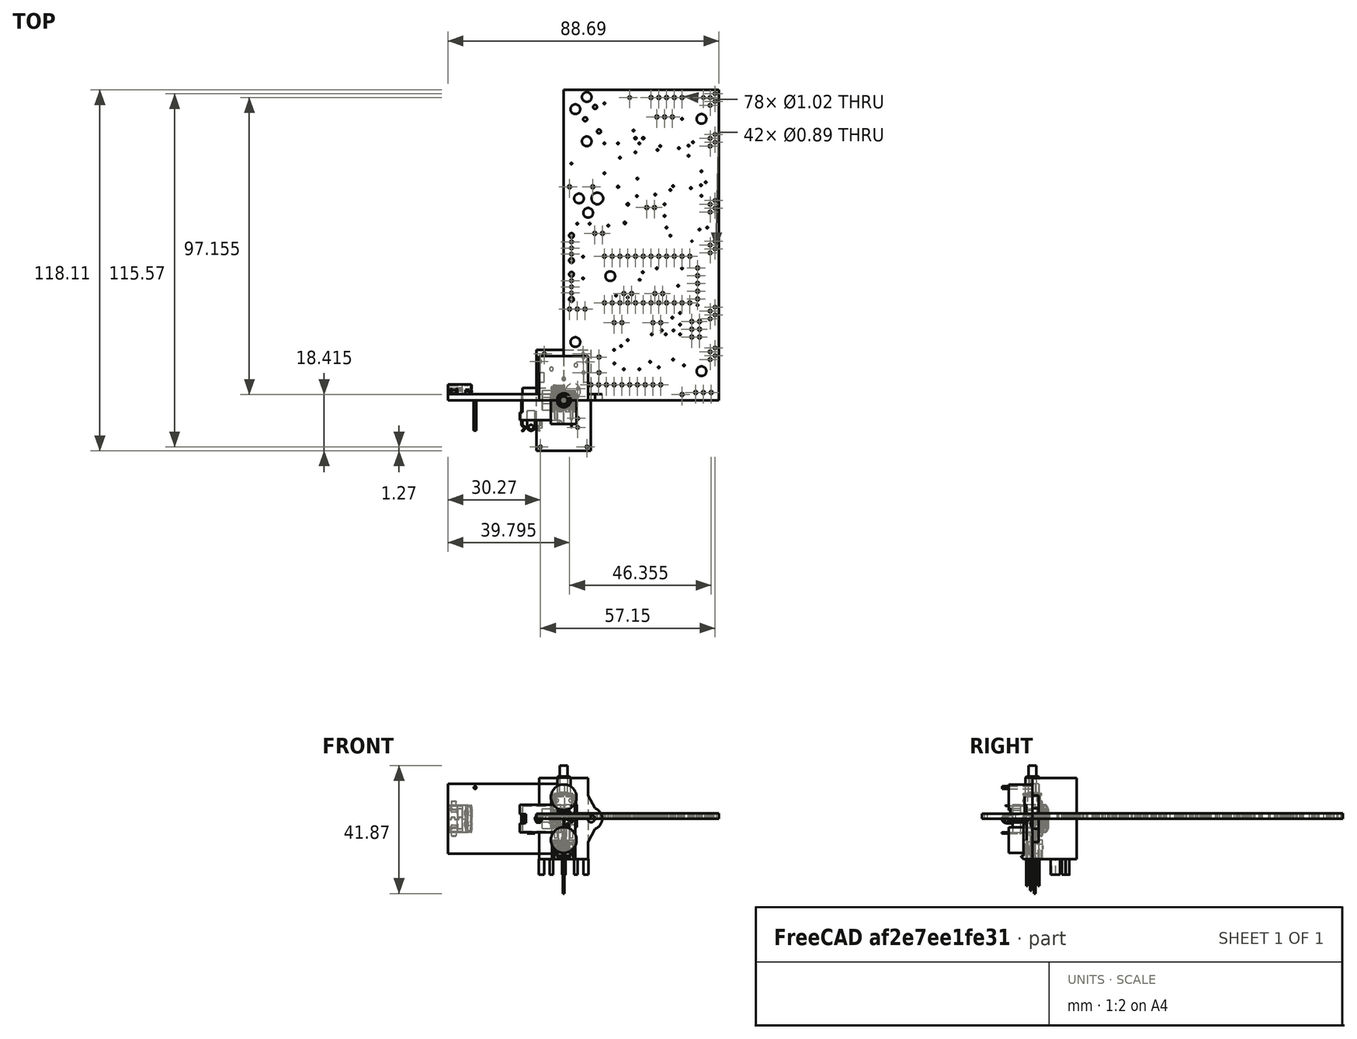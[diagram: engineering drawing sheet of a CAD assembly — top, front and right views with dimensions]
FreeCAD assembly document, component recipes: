
FREECAD ASSEMBLY — COMPONENT RECIPES ("PCB")

This assembly document has 17 components, labeled P0..P16 below (a component is one placed body or linked part). 2 of them carry a construction recipe — the FreeCAD feature program that regenerates the part from scratch, quoted from this document or its linked companion documents; the rest are supplied as boundary geometry only. No exploded tour is included for this assembly.
COMPONENT P0 — geometry summary ("CUI_PJ-202A001"; no construction recipe available for this part):
  bounding box: 14.5 x 14.4 x 9.4 mm
  tessellated surface: 3,812 triangles
  volume: 1019 mm^3 (52% of its bounding box)
COMPONENT P1 — geometry summary ("Dual RCA001"; no construction recipe available for this part):
  bounding box: 31.6 x 22.3 x 20.7 mm
  tessellated surface: 2,744 triangles
  volume: 7146 mm^3 (49% of its bounding box)
COMPONENT P2 — recipe-attached ("Ft232H-2-assembly001", modeled in this document).
Construction recipe (the document's own serialized feature program — sketch geometry with constraints, then the solid features built on it; lengths are millimeters unless a unit is written):

FEATURE [PartDesign::SubShapeBinder] Binder
  BindCopyOnChange = 0
  BindMode = 0
  ClaimChildren = false
  Context = -> Assembly [Ft232H_2_assembly001.Body001.Binder.]
  Fuse = false
  MakeFace = true
  OffsetFill = false
  OffsetIntersection = false
  OffsetJoinType = 0
  OffsetOpenResult = false
  PartialLoad = false
  Refine = true
  Relative = true
  Support = -> [Part__Feature016]
  _Version = 2
FEATURE [Sketcher::SketchObject] Sketch
  ArcFitTolerance = 1e-06
  AttachmentSupport = -> [Binder]
  ExternalGeometry = -> [Binder]
  FullyConstrained = true
  MakeInternals = false
  MapMode = 5
  Placement = pos=(0,-1.32e-13,0) rot=(1,0,0;1.5708rad)
  sketch-geometry (10):
    g0: LineSegment [constr] StartX=-31.5438 StartY=10.16 StartZ=0 EndX=-31.5438 EndY=-10.16 EndZ=0
    g1: LineSegment [constr] StartX=-31.5438 StartY=-10.16 StartZ=0 EndX=-6.14378 EndY=-10.16 EndZ=0
    g2: LineSegment [constr] StartX=-6.14378 StartY=-10.16 StartZ=0 EndX=-6.14378 EndY=10.16 EndZ=0
    g3: LineSegment [constr] StartX=-6.14378 StartY=10.16 StartZ=0 EndX=-31.5438 EndY=10.16 EndZ=0
    g4: GeomPoint [constr] X=-37.8938 Y=-3.968e-13 Z=0
    g5: GeomPoint [constr] X=-31.5438 Y=-3.968e-13 Z=0
    g6: GeomPoint [constr] X=-18.8438 Y=11.43 Z=0
    g7: GeomPoint [constr] X=-18.8438 Y=10.16 Z=0
    g8: Circle [constr] CenterX=-31.5438 CenterY=10.16 CenterZ=0 NormalX=0 NormalY=0 NormalZ=1 AngleXU=0 Radius=0.4445
    g9: Circle CenterX=-29.0038 CenterY=10.16 CenterZ=0 NormalX=0 NormalY=0 NormalZ=1 AngleXU=0 Radius=0.4445
  constraints (23):
    c: DistanceX(g-3,g-1) = 37.8938
    c: Distance(g-3,g-4) = 22.86
    c: Coincident(g1,g2)
    c: Coincident(g2,g3)
    c: Coincident(g3,g0)
    c: Vertical(g0)
    c: Vertical(g2)
    c: Horizontal(g1)
    c: Horizontal(g3)
    c: DistanceX(g3,g3) = 25.4
    c: DistanceY(g2,g2) = 20.32
    c: Symmetric(g-3,g-4,g4)
    c: Symmetric(g0,g0,g5)
    c: Horizontal(g5,g4)
    c: Symmetric(g2,g0,g7)
    c: Symmetric(g-3,g-3,g6)
    c: Vertical(g7,g6)
    c: Coincident(g8,g0)
    c: Diameter(g8) = 0.889
    c: Coincident(g1,g0)
    c: Horizontal(g0,g9)
    c: DistanceX(g0,g9) = 2.54
    c: Equal(g8,g9)
FEATURE [PartDesign::Pad] Pad
  Direction = (0,-1,2e-16)
  Length = 9.906
  Length2 = 10
  Profile = -> Sketch
  ReferenceAxis = -> Sketch [N_Axis]
  Refine = true
  Suppressed = false
  Type = 0
FEATURE [PartDesign::Body] Body001  label="Body"
  AllowCompound = false
  Group = -> [Binder,Sketch,Pad]
  Origin = -> Origin005
  Tip = -> Pad
COMPONENT P3 — geometry summary ("Pro Mini001"; no construction recipe available for this part):
  bounding box: 33.0 x 17.8 x 1.6 mm
  tessellated surface: 2,692 triangles
  volume: 922 mm^3 (99% of its bounding box)
  symmetry: mirror-symmetric across its z mid-plane
COMPONENT P4 — geometry summary ("SLW-864547-5A-RA-D001"; no construction recipe available for this part):
  bounding box: 9.5 x 8.6 x 7.5 mm
  tessellated surface: 1,292 triangles
  volume: 198 mm^3 (32% of its bounding box)
COMPONENT P5 — geometry summary ("SLW-864547-5A-RA-D002"; no construction recipe available for this part):
  bounding box: 9.5 x 8.6 x 7.5 mm
  tessellated surface: 1,292 triangles
  volume: 198 mm^3 (32% of its bounding box)
COMPONENT P6 — geometry summary ("SPST-momentary001"; no construction recipe available for this part):
  bounding box: 18.8 x 11.8 x 8.1 mm
  tessellated surface: 16,178 triangles
  volume: 314 mm^3 (17% of its bounding box)
COMPONENT P7 — geometry summary ("WP154A4SUREQBFZGC001"; no construction recipe available for this part):
  bounding box: 33.1 x 5.9 x 5.4 mm
  tessellated surface: 10,712 triangles
  volume: 191 mm^3 (18% of its bounding box)
  symmetry: mirror-symmetric across its z mid-plane
COMPONENT P8 — geometry summary ("WP154A4SUREQBFZGC002"; no construction recipe available for this part):
  bounding box: 33.1 x 5.9 x 5.4 mm
  tessellated surface: 10,712 triangles
  volume: 191 mm^3 (18% of its bounding box)
  symmetry: mirror-symmetric across its z mid-plane
COMPONENT P9 — geometry summary ("WP154A4SUREQBFZGC003"; no construction recipe available for this part):
  bounding box: 33.1 x 5.9 x 5.4 mm
  tessellated surface: 10,712 triangles
  volume: 191 mm^3 (18% of its bounding box)
  symmetry: mirror-symmetric across its z mid-plane
COMPONENT P10 — geometry summary ("WP154A4SUREQBFZGC004"; no construction recipe available for this part):
  bounding box: 33.1 x 5.9 x 5.4 mm
  tessellated surface: 10,712 triangles
  volume: 191 mm^3 (18% of its bounding box)
  symmetry: mirror-symmetric across its z mid-plane
COMPONENT P11 — geometry summary ("WP154A4SUREQBFZGC005"; no construction recipe available for this part):
  bounding box: 33.1 x 5.9 x 5.4 mm
  tessellated surface: 10,712 triangles
  volume: 191 mm^3 (18% of its bounding box)
  symmetry: mirror-symmetric across its z mid-plane
COMPONENT P12 — geometry summary ("WP154A4SUREQBFZGC006"; no construction recipe available for this part):
  bounding box: 33.1 x 5.9 x 5.4 mm
  tessellated surface: 10,712 triangles
  volume: 191 mm^3 (18% of its bounding box)
  symmetry: mirror-symmetric across its z mid-plane
COMPONENT P13 — geometry summary ("3pinconnector-640441-005"; no construction recipe available for this part):
  bounding box: 13.2 x 7.6 x 7.1 mm
  tessellated surface: 3,348 triangles
  volume: 338 mm^3 (47% of its bounding box)
COMPONENT P14 — geometry summary ("3pinconnector-640441-006"; no construction recipe available for this part):
  bounding box: 13.2 x 7.6 x 7.1 mm
  tessellated surface: 3,348 triangles
  volume: 338 mm^3 (47% of its bounding box)
COMPONENT P15 — geometry summary ("3pinconnector-640441-004"; no construction recipe available for this part):
  bounding box: 13.2 x 7.6 x 7.1 mm
  tessellated surface: 3,348 triangles
  volume: 338 mm^3 (47% of its bounding box)
COMPONENT P16 — recipe-attached ("pcb imported001", modeled in this document).
Construction recipe (the document's own serialized feature program — sketch geometry with constraints, then the solid features built on it; lengths are millimeters unless a unit is written):

FEATURE [Sketcher::SketchObject] MainSketch
  ArcFitTolerance = 1e-06
  AttachmentSupport = -> [XY_Plane]
  FullyConstrained = false
  MakeInternals = false
  MapMode = 5
  sketch-geometry (4):
    g0: LineSegment StartX=0 StartY=0 StartZ=0 EndX=50.8 EndY=0 EndZ=0
    g1: LineSegment StartX=50.8 StartY=0 StartZ=0 EndX=50.8 EndY=101.6 EndZ=0
    g2: LineSegment StartX=50.8 StartY=101.6 StartZ=0 EndX=0 EndY=101.6 EndZ=0
    g3: LineSegment StartX=0 StartY=101.6 StartZ=0 EndX=0 EndY=0 EndZ=0
  constraints (4):
    c: Horizontal(g0)
    c: Horizontal(g2)
    c: Vertical(g1)
    c: Vertical(g3)
FEATURE [PartDesign::Pad] Main
  Direction = (0,0,1)
  Length = 1.778
  Length2 = 100.076
  Profile = -> MainSketch
  Refine = true
  Suppressed = false
  Type = 0
FEATURE [Sketcher::SketchObject] HoleSketch
  ArcFitTolerance = 1e-06
  AttachmentSupport = -> [XY_Plane]
  FullyConstrained = false
  MakeInternals = false
  MapMode = 5
  sketch-geometry (197):
    g0: Circle CenterX=41.275 CenterY=47.117 CenterZ=0 NormalX=0 NormalY=0 NormalZ=1 AngleXU=0 Radius=0.508
    g1: Circle CenterX=38.735 CenterY=47.117 CenterZ=0 NormalX=0 NormalY=0 NormalZ=1 AngleXU=0 Radius=0.508
    g2: Circle CenterX=36.195 CenterY=47.117 CenterZ=0 NormalX=0 NormalY=0 NormalZ=1 AngleXU=0 Radius=0.508
    g3: Circle CenterX=13.335 CenterY=47.117 CenterZ=0 NormalX=0 NormalY=0 NormalZ=1 AngleXU=0 Radius=0.508
    g4: Circle CenterX=33.655 CenterY=47.117 CenterZ=0 NormalX=0 NormalY=0 NormalZ=1 AngleXU=0 Radius=0.508
    g5: Circle CenterX=15.875 CenterY=47.117 CenterZ=0 NormalX=0 NormalY=0 NormalZ=1 AngleXU=0 Radius=0.508
    g6: Circle CenterX=31.115 CenterY=47.117 CenterZ=0 NormalX=0 NormalY=0 NormalZ=1 AngleXU=0 Radius=0.508
    g7: Circle CenterX=28.575 CenterY=47.117 CenterZ=0 NormalX=0 NormalY=0 NormalZ=1 AngleXU=0 Radius=0.508
    g8: Circle CenterX=26.035 CenterY=47.117 CenterZ=0 NormalX=0 NormalY=0 NormalZ=1 AngleXU=0 Radius=0.508
    g9: Circle CenterX=18.415 CenterY=47.117 CenterZ=0 NormalX=0 NormalY=0 NormalZ=1 AngleXU=0 Radius=0.508
    g10: Circle CenterX=20.955 CenterY=47.117 CenterZ=0 NormalX=0 NormalY=0 NormalZ=1 AngleXU=0 Radius=0.508
    g11: Circle CenterX=23.495 CenterY=47.117 CenterZ=0 NormalX=0 NormalY=0 NormalZ=1 AngleXU=0 Radius=0.508
    g12: Circle CenterX=15.875 CenterY=31.877 CenterZ=0 NormalX=0 NormalY=0 NormalZ=1 AngleXU=0 Radius=0.508
    g13: Circle CenterX=13.335 CenterY=31.877 CenterZ=0 NormalX=0 NormalY=0 NormalZ=1 AngleXU=0 Radius=0.508
    g14: Circle CenterX=20.955 CenterY=31.877 CenterZ=0 NormalX=0 NormalY=0 NormalZ=1 AngleXU=0 Radius=0.508
    g15: Circle CenterX=18.415 CenterY=31.877 CenterZ=0 NormalX=0 NormalY=0 NormalZ=1 AngleXU=0 Radius=0.508
    g16: Circle CenterX=26.035 CenterY=31.877 CenterZ=0 NormalX=0 NormalY=0 NormalZ=1 AngleXU=0 Radius=0.508
    g17: Circle CenterX=23.495 CenterY=31.877 CenterZ=0 NormalX=0 NormalY=0 NormalZ=1 AngleXU=0 Radius=0.508
    g18: Circle CenterX=31.115 CenterY=31.877 CenterZ=0 NormalX=0 NormalY=0 NormalZ=1 AngleXU=0 Radius=0.508
    g19: Circle CenterX=28.575 CenterY=31.877 CenterZ=0 NormalX=0 NormalY=0 NormalZ=1 AngleXU=0 Radius=0.508
    g20: Circle CenterX=36.195 CenterY=31.877 CenterZ=0 NormalX=0 NormalY=0 NormalZ=1 AngleXU=0 Radius=0.508
    g21: Circle CenterX=33.655 CenterY=31.877 CenterZ=0 NormalX=0 NormalY=0 NormalZ=1 AngleXU=0 Radius=0.508
    g22: Circle CenterX=41.275 CenterY=31.877 CenterZ=0 NormalX=0 NormalY=0 NormalZ=1 AngleXU=0 Radius=0.508
    g23: Circle CenterX=38.735 CenterY=31.877 CenterZ=0 NormalX=0 NormalY=0 NormalZ=1 AngleXU=0 Radius=0.508
    g24: Circle CenterX=22.225 CenterY=34.925 CenterZ=0 NormalX=0 NormalY=0 NormalZ=1 AngleXU=0 Radius=0.508
    g25: Circle CenterX=19.685 CenterY=34.925 CenterZ=0 NormalX=0 NormalY=0 NormalZ=1 AngleXU=0 Radius=0.508
    g26: Circle CenterX=32.385 CenterY=34.925 CenterZ=0 NormalX=0 NormalY=0 NormalZ=1 AngleXU=0 Radius=0.508
    g27: Circle CenterX=29.845 CenterY=34.925 CenterZ=0 NormalX=0 NormalY=0 NormalZ=1 AngleXU=0 Radius=0.508
    g28: Circle CenterX=43.815 CenterY=43.307 CenterZ=0 NormalX=0 NormalY=0 NormalZ=1 AngleXU=0 Radius=0.508
    g29: Circle CenterX=43.815 CenterY=40.767 CenterZ=0 NormalX=0 NormalY=0 NormalZ=1 AngleXU=0 Radius=0.508
    g30: Circle CenterX=43.815 CenterY=38.227 CenterZ=0 NormalX=0 NormalY=0 NormalZ=1 AngleXU=0 Radius=0.508
    g31: Circle CenterX=43.815 CenterY=35.687 CenterZ=0 NormalX=0 NormalY=0 NormalZ=1 AngleXU=0 Radius=0.508
    g32: Circle CenterX=43.815 CenterY=33.147 CenterZ=0 NormalX=0 NormalY=0 NormalZ=1 AngleXU=0 Radius=0.508
    g33: Circle CenterX=16.51 CenterY=25.4 CenterZ=0 NormalX=0 NormalY=0 NormalZ=1 AngleXU=0 Radius=0.508
    g34: Circle CenterX=8.89 CenterY=5.08 CenterZ=0 NormalX=0 NormalY=0 NormalZ=1 AngleXU=0 Radius=0.508
    g35: Circle CenterX=19.05 CenterY=25.4 CenterZ=0 NormalX=0 NormalY=0 NormalZ=1 AngleXU=0 Radius=0.508
    g36: Circle CenterX=11.43 CenterY=5.08 CenterZ=0 NormalX=0 NormalY=0 NormalZ=1 AngleXU=0 Radius=0.508
    g37: Circle CenterX=13.97 CenterY=5.08 CenterZ=0 NormalX=0 NormalY=0 NormalZ=1 AngleXU=0 Radius=0.508
    g38: Circle CenterX=16.51 CenterY=5.08 CenterZ=0 NormalX=0 NormalY=0 NormalZ=1 AngleXU=0 Radius=0.508
    g39: Circle CenterX=19.05 CenterY=5.08 CenterZ=0 NormalX=0 NormalY=0 NormalZ=1 AngleXU=0 Radius=0.508
    g40: Circle CenterX=21.59 CenterY=5.08 CenterZ=0 NormalX=0 NormalY=0 NormalZ=1 AngleXU=0 Radius=0.508
    g41: Circle CenterX=24.13 CenterY=5.08 CenterZ=0 NormalX=0 NormalY=0 NormalZ=1 AngleXU=0 Radius=0.508
    g42: Circle CenterX=26.67 CenterY=5.08 CenterZ=0 NormalX=0 NormalY=0 NormalZ=1 AngleXU=0 Radius=0.508
    g43: Circle CenterX=29.21 CenterY=25.4 CenterZ=0 NormalX=0 NormalY=0 NormalZ=1 AngleXU=0 Radius=0.508
    g44: Circle CenterX=29.21 CenterY=5.08 CenterZ=0 NormalX=0 NormalY=0 NormalZ=1 AngleXU=0 Radius=0.508
    g45: Circle CenterX=31.75 CenterY=25.4 CenterZ=0 NormalX=0 NormalY=0 NormalZ=1 AngleXU=0 Radius=0.508
    g46: Circle CenterX=31.75 CenterY=5.08 CenterZ=0 NormalX=0 NormalY=0 NormalZ=1 AngleXU=0 Radius=0.508
    g47: Circle CenterX=11.5358 CenterY=9.05933 CenterZ=0 NormalX=0 NormalY=0 NormalZ=1 AngleXU=0 Radius=0.508
    g48: Circle CenterX=11.5358 CenterY=14.1393 CenterZ=0 NormalX=0 NormalY=0 NormalZ=1 AngleXU=0 Radius=0.508
    g49: Circle CenterX=6.45583 CenterY=9.05933 CenterZ=0 NormalX=0 NormalY=0 NormalZ=1 AngleXU=0 Radius=0.508
    g50: Circle CenterX=6.45583 CenterY=14.1393 CenterZ=0 NormalX=0 NormalY=0 NormalZ=1 AngleXU=0 Radius=0.508
    g51: Circle CenterX=6.985 CenterY=29.845 CenterZ=0 NormalX=0 NormalY=0 NormalZ=1 AngleXU=0 Radius=0.508
    g52: Circle CenterX=4.445 CenterY=29.845 CenterZ=0 NormalX=0 NormalY=0 NormalZ=1 AngleXU=0 Radius=0.508
    g53: Circle CenterX=1.905 CenterY=29.845 CenterZ=0 NormalX=0 NormalY=0 NormalZ=1 AngleXU=0 Radius=0.508
    g54: Circle CenterX=44.45 CenterY=25.781 CenterZ=0 NormalX=0 NormalY=0 NormalZ=1 AngleXU=0 Radius=0.508
    g55: Circle CenterX=44.45 CenterY=23.241 CenterZ=0 NormalX=0 NormalY=0 NormalZ=1 AngleXU=0 Radius=0.508
    g56: Circle CenterX=44.45 CenterY=20.701 CenterZ=0 NormalX=0 NormalY=0 NormalZ=1 AngleXU=0 Radius=0.508
    g57: Circle CenterX=41.91 CenterY=25.781 CenterZ=0 NormalX=0 NormalY=0 NormalZ=1 AngleXU=0 Radius=0.508
    g58: Circle CenterX=41.91 CenterY=23.241 CenterZ=0 NormalX=0 NormalY=0 NormalZ=1 AngleXU=0 Radius=0.508
    g59: Circle CenterX=41.91 CenterY=20.701 CenterZ=0 NormalX=0 NormalY=0 NormalZ=1 AngleXU=0 Radius=0.508
    g60: Circle CenterX=43.18 CenterY=2.54 CenterZ=0 NormalX=0 NormalY=0 NormalZ=1 AngleXU=0 Radius=0.508
    g61: Circle CenterX=45.72 CenterY=2.54 CenterZ=0 NormalX=0 NormalY=0 NormalZ=1 AngleXU=0 Radius=0.508
    g62: Circle CenterX=48.26 CenterY=2.54 CenterZ=0 NormalX=0 NormalY=0 NormalZ=1 AngleXU=0 Radius=0.508
    g63: Circle CenterX=28.575 CenterY=99.06 CenterZ=0 NormalX=0 NormalY=0 NormalZ=1 AngleXU=0 Radius=0.508
    g64: Circle CenterX=31.115 CenterY=99.06 CenterZ=0 NormalX=0 NormalY=0 NormalZ=1 AngleXU=0 Radius=0.508
    g65: Circle CenterX=38.735 CenterY=99.06 CenterZ=0 NormalX=0 NormalY=0 NormalZ=1 AngleXU=0 Radius=0.508
    g66: Circle CenterX=36.195 CenterY=99.06 CenterZ=0 NormalX=0 NormalY=0 NormalZ=1 AngleXU=0 Radius=0.508
    g67: Circle CenterX=10.16 CenterY=54.61 CenterZ=0 NormalX=0 NormalY=0 NormalZ=1 AngleXU=0 Radius=0.508
    g68: Circle CenterX=12.7 CenterY=54.61 CenterZ=0 NormalX=0 NormalY=0 NormalZ=1 AngleXU=0 Radius=0.508
    g69: Circle CenterX=13.335 CenterY=97.155 CenterZ=0 NormalX=0 NormalY=0 NormalZ=1 AngleXU=0 Radius=0.254
    g70: Circle CenterX=46.5032 CenterY=71.3317 CenterZ=0 NormalX=0 NormalY=0 NormalZ=1 AngleXU=0 Radius=0.254
    g71: Circle CenterX=30.48 CenterY=92.71 CenterZ=0 NormalX=0 NormalY=0 NormalZ=1 AngleXU=0 Radius=0.508
    g72: Circle CenterX=33.02 CenterY=92.71 CenterZ=0 NormalX=0 NormalY=0 NormalZ=1 AngleXU=0 Radius=0.508
    g73: Circle CenterX=35.56 CenterY=92.71 CenterZ=0 NormalX=0 NormalY=0 NormalZ=1 AngleXU=0 Radius=0.508
    g74: Circle CenterX=45.085 CenterY=66.8867 CenterZ=0 NormalX=0 NormalY=0 NormalZ=1 AngleXU=0 Radius=0.254
    g75: Circle CenterX=25.8445 CenterY=41.91 CenterZ=0 NormalX=0 NormalY=0 NormalZ=1 AngleXU=0 Radius=0.254
    g76: Circle CenterX=44.9157 CenterY=70.4003 CenterZ=0 NormalX=0 NormalY=0 NormalZ=1 AngleXU=0 Radius=0.254
    g77: Circle CenterX=41.6348 CenterY=69.4055 CenterZ=0 NormalX=0 NormalY=0 NormalZ=1 AngleXU=0 Radius=0.254
    g78: Circle CenterX=33.655 CenterY=56.515 CenterZ=0 NormalX=0 NormalY=0 NormalZ=1 AngleXU=0 Radius=0.254
    g79: Circle CenterX=34.925 CenterY=53.8903 CenterZ=0 NormalX=0 NormalY=0 NormalZ=1 AngleXU=0 Radius=0.254
    g80: Circle CenterX=17.78 CenterY=84.074 CenterZ=0 NormalX=0 NormalY=0 NormalZ=1 AngleXU=0 Radius=0.254
    g81: Circle CenterX=38.735 CenterY=43.18 CenterZ=0 NormalX=0 NormalY=0 NormalZ=1 AngleXU=0 Radius=0.254
    g82: Circle CenterX=30.48 CenterY=43.18 CenterZ=0 NormalX=0 NormalY=0 NormalZ=1 AngleXU=0 Radius=0.254
    g83: Circle CenterX=24.8708 CenterY=39.4123 CenterZ=0 NormalX=0 NormalY=0 NormalZ=1 AngleXU=0 Radius=0.254
    g84: Circle CenterX=34.925 CenterY=68.7917 CenterZ=0 NormalX=0 NormalY=0 NormalZ=1 AngleXU=0 Radius=0.254
    g85: Circle CenterX=45.72 CenterY=99.06 CenterZ=0 NormalX=0 NormalY=0 NormalZ=1 AngleXU=0 Radius=0.4445
    g86: Circle CenterX=33.02 CenterY=60.325 CenterZ=0 NormalX=0 NormalY=0 NormalZ=1 AngleXU=0 Radius=0.254
    g87: Circle CenterX=38.735 CenterY=1.905 CenterZ=0 NormalX=0 NormalY=0 NormalZ=1 AngleXU=0 Radius=0.508
    g88: Circle CenterX=29.6968 CenterY=63.0555 CenterZ=0 NormalX=0 NormalY=0 NormalZ=1 AngleXU=0 Radius=0.508
    g89: Circle CenterX=27.1568 CenterY=63.0555 CenterZ=0 NormalX=0 NormalY=0 NormalZ=1 AngleXU=0 Radius=0.508
    g90: Circle CenterX=17.78 CenterY=69.85 CenterZ=0 NormalX=0 NormalY=0 NormalZ=1 AngleXU=0 Radius=0.3175
    g91: Circle CenterX=29.9508 CenterY=67.3312 CenterZ=0 NormalX=0 NormalY=0 NormalZ=1 AngleXU=0 Radius=0.254
    g92: Circle CenterX=23.9183 CenterY=66.8232 CenterZ=0 NormalX=0 NormalY=0 NormalZ=1 AngleXU=0 Radius=0.254
    g93: Circle CenterX=4.99533 CenterY=66.04 CenterZ=0 NormalX=0 NormalY=0 NormalZ=1 AngleXU=0 Radius=1.5875
    g94: Circle CenterX=11.0067 CenterY=66.04 CenterZ=0 NormalX=0 NormalY=0 NormalZ=1 AngleXU=0 Radius=1.905
    g95: Circle CenterX=8.001 CenterY=61.341 CenterZ=0 NormalX=0 NormalY=0 NormalZ=1 AngleXU=0 Radius=1.5875
    g96: Circle CenterX=11.5358 CenterY=87.9687 CenterZ=0 NormalX=0 NormalY=0 NormalZ=1 AngleXU=0 Radius=0.656167
    g97: Circle CenterX=10.2764 CenterY=95.9697 CenterZ=0 NormalX=0 NormalY=0 NormalZ=1 AngleXU=0 Radius=0.661458
    g98: Circle CenterX=7.02733 CenterY=91.9692 CenterZ=0 NormalX=0 NormalY=0 NormalZ=1 AngleXU=0 Radius=0.656167
    g99: Circle CenterX=7.53533 CenterY=84.7302 CenterZ=0 NormalX=0 NormalY=0 NormalZ=1 AngleXU=0 Radius=1.5875
    g100: Circle CenterX=7.53533 CenterY=99.2293 CenterZ=0 NormalX=0 NormalY=0 NormalZ=1 AngleXU=0 Radius=1.5875
    g101: Circle CenterX=13.335 CenterY=84.0528 CenterZ=0 NormalX=0 NormalY=0 NormalZ=1 AngleXU=0 Radius=0.254
    g102: Circle CenterX=33.02 CenterY=64.135 CenterZ=0 NormalX=0 NormalY=0 NormalZ=1 AngleXU=0 Radius=0.254
    g103: Circle CenterX=17.145 CenterY=34.29 CenterZ=0 NormalX=0 NormalY=0 NormalZ=1 AngleXU=0 Radius=0.254
    g104: Circle CenterX=38.1 CenterY=21.59 CenterZ=0 NormalX=0 NormalY=0 NormalZ=1 AngleXU=0 Radius=0.254
    g105: Circle CenterX=35.56 CenterY=27.0722 CenterZ=0 NormalX=0 NormalY=0 NormalZ=1 AngleXU=0 Radius=0.254
    g106: Circle CenterX=38.1 CenterY=24.765 CenterZ=0 NormalX=0 NormalY=0 NormalZ=1 AngleXU=0 Radius=0.254
    g107: Circle CenterX=38.1 CenterY=28.575 CenterZ=0 NormalX=0 NormalY=0 NormalZ=1 AngleXU=0 Radius=0.254
    g108: Circle CenterX=20.955 CenterY=33.655 CenterZ=0 NormalX=0 NormalY=0 NormalZ=1 AngleXU=0 Radius=0.254
    g109: Circle CenterX=43.815 CenterY=31.115 CenterZ=0 NormalX=0 NormalY=0 NormalZ=1 AngleXU=0 Radius=0.254
    g110: Circle CenterX=45.085 CenterY=9.525 CenterZ=0 NormalX=0 NormalY=0 NormalZ=1 AngleXU=0 Radius=1.5875
    g111: Circle CenterX=45.085 CenterY=92.075 CenterZ=0 NormalX=0 NormalY=0 NormalZ=1 AngleXU=0 Radius=1.5875
    g112: Circle CenterX=35.814 CenterY=70.0617 CenterZ=0 NormalX=0 NormalY=0 NormalZ=1 AngleXU=0 Radius=0.254
    g113: Circle CenterX=3.81 CenterY=95.25 CenterZ=0 NormalX=0 NormalY=0 NormalZ=1 AngleXU=0 Radius=1.5875
    g114: Circle CenterX=37.465 CenterY=37.465 CenterZ=0 NormalX=0 NormalY=0 NormalZ=1 AngleXU=0 Radius=0.254
    g115: Circle CenterX=21.59 CenterY=99.06 CenterZ=0 NormalX=0 NormalY=0 NormalZ=1 AngleXU=0 Radius=0.4445
    g116: Circle CenterX=35.814 CenterY=13.335 CenterZ=0 NormalX=0 NormalY=0 NormalZ=1 AngleXU=0 Radius=0.254
    g117: Circle CenterX=28.829 CenterY=21.59 CenterZ=0 NormalX=0 NormalY=0 NormalZ=1 AngleXU=0 Radius=0.254
    g118: Circle CenterX=33.401 CenterY=21.59 CenterZ=0 NormalX=0 NormalY=0 NormalZ=1 AngleXU=0 Radius=0.254
    g119: Circle CenterX=35.941 CenterY=22.86 CenterZ=0 NormalX=0 NormalY=0 NormalZ=1 AngleXU=0 Radius=0.254
    g120: Circle CenterX=32.131 CenterY=22.86 CenterZ=0 NormalX=0 NormalY=0 NormalZ=1 AngleXU=0 Radius=0.254
    g121: Circle CenterX=18.796 CenterY=17.7377 CenterZ=0 NormalX=0 NormalY=0 NormalZ=1 AngleXU=0 Radius=0.254
    g122: Circle CenterX=28.2575 CenterY=12.5942 CenterZ=0 NormalX=0 NormalY=0 NormalZ=1 AngleXU=0 Radius=0.254
    g123: Circle CenterX=20.955 CenterY=19.685 CenterZ=0 NormalX=0 NormalY=0 NormalZ=1 AngleXU=0 Radius=0.254
    g124: Circle CenterX=24.765 CenterY=10.16 CenterZ=0 NormalX=0 NormalY=0 NormalZ=1 AngleXU=0 Radius=0.254
    g125: Circle CenterX=16.5523 CenterY=12.065 CenterZ=0 NormalX=0 NormalY=0 NormalZ=1 AngleXU=0 Radius=0.254
    g126: Circle CenterX=16.4888 CenterY=16.51 CenterZ=0 NormalX=0 NormalY=0 NormalZ=1 AngleXU=0 Radius=0.254
    g127: Circle CenterX=19.685 CenterY=10.16 CenterZ=0 NormalX=0 NormalY=0 NormalZ=1 AngleXU=0 Radius=0.254
    g128: Circle CenterX=39.37 CenterY=11.43 CenterZ=0 NormalX=0 NormalY=0 NormalZ=1 AngleXU=0 Radius=0.254
    g129: Circle CenterX=33.655 CenterY=99.06 CenterZ=0 NormalX=0 NormalY=0 NormalZ=1 AngleXU=0 Radius=0.508
    g130: Circle CenterX=3.81 CenterY=19.05 CenterZ=0 NormalX=0 NormalY=0 NormalZ=1 AngleXU=0 Radius=1.5875
    g131: Circle CenterX=15.24 CenterY=40.6188 CenterZ=0 NormalX=0 NormalY=0 NormalZ=1 AngleXU=0 Radius=1.5875
    g132: Circle CenterX=42.3122 CenterY=84.455 CenterZ=0 NormalX=0 NormalY=0 NormalZ=1 AngleXU=0 Radius=0.254
    g133: Circle CenterX=40.8517 CenterY=80.01 CenterZ=0 NormalX=0 NormalY=0 NormalZ=1 AngleXU=0 Radius=0.254
    g134: Circle CenterX=40.8517 CenterY=83.3332 CenterZ=0 NormalX=0 NormalY=0 NormalZ=1 AngleXU=0 Radius=0.254
    g135: Circle CenterX=37.6767 CenterY=82.4865 CenterZ=0 NormalX=0 NormalY=0 NormalZ=1 AngleXU=0 Radius=0.254
    g136: Circle CenterX=30.6917 CenterY=81.915 CenterZ=0 NormalX=0 NormalY=0 NormalZ=1 AngleXU=0 Radius=0.254
    g137: Circle CenterX=31.5807 CenterY=83.185 CenterZ=0 NormalX=0 NormalY=0 NormalZ=1 AngleXU=0 Radius=0.254
    g138: Circle CenterX=38.735 CenterY=92.075 CenterZ=0 NormalX=0 NormalY=0 NormalZ=1 AngleXU=0 Radius=0.254
    g139: Circle CenterX=3.048 CenterY=3.048 CenterZ=0 NormalX=0 NormalY=0 NormalZ=1 AngleXU=0 Radius=2.43417
    g140: Circle CenterX=2.54 CenterY=77.47 CenterZ=0 NormalX=0 NormalY=0 NormalZ=1 AngleXU=0 Radius=0.254
    g141: Circle CenterX=26.0244 CenterY=85.7673 CenterZ=0 NormalX=0 NormalY=0 NormalZ=1 AngleXU=0 Radius=0.365125
    g142: Circle CenterX=23.4844 CenterY=85.7673 CenterZ=0 NormalX=0 NormalY=0 NormalZ=1 AngleXU=0 Radius=0.365125
    g143: Circle CenterX=24.765 CenterY=84.0317 CenterZ=0 NormalX=0 NormalY=0 NormalZ=1 AngleXU=0 Radius=0.254
    g144: Circle CenterX=18.415 CenterY=79.375 CenterZ=0 NormalX=0 NormalY=0 NormalZ=1 AngleXU=0 Radius=0.254
    g145: Circle CenterX=23.495 CenterY=81.1318 CenterZ=0 NormalX=0 NormalY=0 NormalZ=1 AngleXU=0 Radius=0.254
    g146: Circle CenterX=2.56117 CenterY=51.8372 CenterZ=0 NormalX=0 NormalY=0 NormalZ=1 AngleXU=0 Radius=0.4445
    g147: Circle CenterX=2.56117 CenterY=47.8367 CenterZ=0 NormalX=0 NormalY=0 NormalZ=1 AngleXU=0 Radius=0.4445
    g148: Circle CenterX=2.55058 CenterY=45.7306 CenterZ=0 NormalX=0 NormalY=0 NormalZ=1 AngleXU=0 Radius=0.772583
    g149: Circle CenterX=2.55058 CenterY=53.9221 CenterZ=0 NormalX=0 NormalY=0 NormalZ=1 AngleXU=0 Radius=0.772583
    g150: Circle CenterX=2.56117 CenterY=49.8263 CenterZ=0 NormalX=0 NormalY=0 NormalZ=1 AngleXU=0 Radius=0.4445
    g151: Circle CenterX=2.56117 CenterY=39.1372 CenterZ=0 NormalX=0 NormalY=0 NormalZ=1 AngleXU=0 Radius=0.4445
    g152: Circle CenterX=2.56117 CenterY=35.1367 CenterZ=0 NormalX=0 NormalY=0 NormalZ=1 AngleXU=0 Radius=0.4445
    g153: Circle CenterX=2.55058 CenterY=33.0306 CenterZ=0 NormalX=0 NormalY=0 NormalZ=1 AngleXU=0 Radius=0.772583
    g154: Circle CenterX=2.55058 CenterY=41.2327 CenterZ=0 NormalX=0 NormalY=0 NormalZ=1 AngleXU=0 Radius=0.777875
    g155: Circle CenterX=2.56117 CenterY=37.1263 CenterZ=0 NormalX=0 NormalY=0 NormalZ=1 AngleXU=0 Radius=0.4445
    g156: Circle CenterX=22.86 CenterY=88.265 CenterZ=0 NormalX=0 NormalY=0 NormalZ=1 AngleXU=0 Radius=0.254
    g157: Circle CenterX=6.35 CenterY=39.9203 CenterZ=0 NormalX=0 NormalY=0 NormalZ=1 AngleXU=0 Radius=0.254
    g158: Circle CenterX=31.115 CenterY=10.795 CenterZ=0 NormalX=0 NormalY=0 NormalZ=1 AngleXU=0 Radius=0.254
    g159: Circle CenterX=20.0025 CenterY=58.0496 CenterZ=0 NormalX=0 NormalY=0 NormalZ=1 AngleXU=0 Radius=0.365125
    g160: Circle CenterX=4.445 CenterY=57.785 CenterZ=0 NormalX=0 NormalY=0 NormalZ=1 AngleXU=0 Radius=0.254
    g161: Circle CenterX=6.35 CenterY=46.99 CenterZ=0 NormalX=0 NormalY=0 NormalZ=1 AngleXU=0 Radius=0.254
    g162: Circle CenterX=8.509 CenterY=57.8062 CenterZ=0 NormalX=0 NormalY=0 NormalZ=1 AngleXU=0 Radius=0.254
    g163: Circle CenterX=14.605 CenterY=57.15 CenterZ=0 NormalX=0 NormalY=0 NormalZ=1 AngleXU=0 Radius=0.254
    g164: Circle CenterX=24.13 CenterY=72.5593 CenterZ=0 NormalX=0 NormalY=0 NormalZ=1 AngleXU=0 Radius=0.254
    g165: Circle CenterX=13.335 CenterY=74.295 CenterZ=0 NormalX=0 NormalY=0 NormalZ=1 AngleXU=0 Radius=0.254
    g166: Circle CenterX=20.9444 CenterY=64.1244 CenterZ=0 NormalX=0 NormalY=0 NormalZ=1 AngleXU=0 Radius=0.370417
    g167: Circle CenterX=9.525 CenterY=69.85 CenterZ=0 NormalX=0 NormalY=0 NormalZ=1 AngleXU=0 Radius=0.508
    g168: Circle CenterX=1.905 CenterY=69.85 CenterZ=0 NormalX=0 NormalY=0 NormalZ=1 AngleXU=0 Radius=0.508
    g169: Circle CenterX=49.53 CenterY=100.33 CenterZ=0 NormalX=0 NormalY=0 NormalZ=1 AngleXU=0 Radius=0.4445
    g170: Circle CenterX=47.9213 CenterY=99.06 CenterZ=0 NormalX=0 NormalY=0 NormalZ=1 AngleXU=0 Radius=0.4445
    g171: Circle CenterX=49.53 CenterY=97.79 CenterZ=0 NormalX=0 NormalY=0 NormalZ=1 AngleXU=0 Radius=0.4445
    g172: Circle CenterX=47.9213 CenterY=96.52 CenterZ=0 NormalX=0 NormalY=0 NormalZ=1 AngleXU=0 Radius=0.4445
    g173: Circle CenterX=49.53 CenterY=86.995 CenterZ=0 NormalX=0 NormalY=0 NormalZ=1 AngleXU=0 Radius=0.4445
    g174: Circle CenterX=47.9213 CenterY=85.725 CenterZ=0 NormalX=0 NormalY=0 NormalZ=1 AngleXU=0 Radius=0.4445
    g175: Circle CenterX=49.53 CenterY=84.455 CenterZ=0 NormalX=0 NormalY=0 NormalZ=1 AngleXU=0 Radius=0.4445
    g176: Circle CenterX=47.9213 CenterY=83.185 CenterZ=0 NormalX=0 NormalY=0 NormalZ=1 AngleXU=0 Radius=0.4445
    g177: Circle CenterX=49.53 CenterY=65.405 CenterZ=0 NormalX=0 NormalY=0 NormalZ=1 AngleXU=0 Radius=0.4445
    g178: Circle CenterX=47.9213 CenterY=64.135 CenterZ=0 NormalX=0 NormalY=0 NormalZ=1 AngleXU=0 Radius=0.4445
    g179: Circle CenterX=49.53 CenterY=62.865 CenterZ=0 NormalX=0 NormalY=0 NormalZ=1 AngleXU=0 Radius=0.4445
    g180: Circle CenterX=47.9213 CenterY=61.595 CenterZ=0 NormalX=0 NormalY=0 NormalZ=1 AngleXU=0 Radius=0.4445
    g181: Circle CenterX=49.53 CenterY=52.07 CenterZ=0 NormalX=0 NormalY=0 NormalZ=1 AngleXU=0 Radius=0.4445
    g182: Circle CenterX=47.9213 CenterY=50.8 CenterZ=0 NormalX=0 NormalY=0 NormalZ=1 AngleXU=0 Radius=0.4445
    g183: Circle CenterX=49.53 CenterY=49.53 CenterZ=0 NormalX=0 NormalY=0 NormalZ=1 AngleXU=0 Radius=0.4445
    g184: Circle CenterX=47.9213 CenterY=48.26 CenterZ=0 NormalX=0 NormalY=0 NormalZ=1 AngleXU=0 Radius=0.4445
    g185: Circle CenterX=49.53 CenterY=30.48 CenterZ=0 NormalX=0 NormalY=0 NormalZ=1 AngleXU=0 Radius=0.4445
    g186: Circle CenterX=47.9213 CenterY=29.21 CenterZ=0 NormalX=0 NormalY=0 NormalZ=1 AngleXU=0 Radius=0.4445
    g187: Circle CenterX=49.53 CenterY=27.94 CenterZ=0 NormalX=0 NormalY=0 NormalZ=1 AngleXU=0 Radius=0.4445
    g188: Circle CenterX=47.9213 CenterY=26.67 CenterZ=0 NormalX=0 NormalY=0 NormalZ=1 AngleXU=0 Radius=0.4445
    g189: Circle CenterX=49.53 CenterY=17.145 CenterZ=0 NormalX=0 NormalY=0 NormalZ=1 AngleXU=0 Radius=0.4445
    g190: Circle CenterX=47.9213 CenterY=15.875 CenterZ=0 NormalX=0 NormalY=0 NormalZ=1 AngleXU=0 Radius=0.4445
    g191: Circle CenterX=49.53 CenterY=14.605 CenterZ=0 NormalX=0 NormalY=0 NormalZ=1 AngleXU=0 Radius=0.4445
    g192: Circle CenterX=47.9213 CenterY=13.335 CenterZ=0 NormalX=0 NormalY=0 NormalZ=1 AngleXU=0 Radius=0.4445
    g193: Circle CenterX=45.085 CenterY=74.93 CenterZ=0 NormalX=0 NormalY=0 NormalZ=1 AngleXU=0 Radius=0.254
    g194: Circle CenterX=46.99 CenterY=56.515 CenterZ=0 NormalX=0 NormalY=0 NormalZ=1 AngleXU=0 Radius=0.254
    g195: Circle CenterX=44.45 CenterY=55.88 CenterZ=0 NormalX=0 NormalY=0 NormalZ=1 AngleXU=0 Radius=0.254
    g196: Circle CenterX=41.9206 CenterY=52.07 CenterZ=0 NormalX=0 NormalY=0 NormalZ=1 AngleXU=0 Radius=0.174625
FEATURE [PartDesign::Pocket] Holes
  BaseFeature = -> Main
  Direction = (0,0,-1)
  Length = 3.556
  Length2 = 5
  Profile = -> HoleSketch
  Refine = true
  Reversed = true
  Suppressed = false
  Type = 0
FEATURE [PartDesign::Body] Body  label="pcb imported"
  AllowCompound = false
  Group = -> [MainSketch,Main,HoleSketch,Holes]
  Origin = -> Origin
  Tip = -> Holes
PROVENANCE & LICENSES
A FreeCAD (.FCStd) document from a public repository crawl; recipes are the document's own serialized feature recipes (and, for linked parts, companion documents' recipes).
License: mit.
